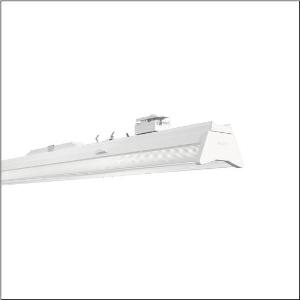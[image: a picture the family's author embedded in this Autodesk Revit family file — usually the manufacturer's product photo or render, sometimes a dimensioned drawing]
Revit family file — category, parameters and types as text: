
# Revit family: licross_r__21_performance_mo_52td167n485g_efc6
name_source: partatom
category: Lighting Fixtures
units: mm (PartAtom-declared; Revit-internal decimal feet)

## family parameters
Cut with Voids When Loaded = No
Host = Face
Light Source = No
Part Type = Normal
Room Calculation Point = No
Round Connector Dimension = Use Diameter
Shared = No

## types (1)
- Licross® 21 Performance MO (1 x LED, 8720 lm, 47.9 W, 4000K)
    Apparent Load = 48 VA
    CIE Flux Codes = 66 88 96 79 100
    Color Rendering = 80
    Color Temperature = 4000K
    Default Elevation = 1800 mm
    Description = Licross® 21 Performance MO, luminaire insert, of sheet steel, galvanised, coil coated, white, length: 1.500mm, width: 120mm, height: 123mm, LED rated luminous flux: 8.720lm, light colour: 840, control gear: ON/OFF, with plug, 3-pole, with phase selection, mains connection: 220..240V, AC, 50/60Hz, rated input power: 48W, halogen-free wiring, primary light control with lens, of plastic, primary optical cover: cover, of PMMA, light emission: direct/indirect distribution, primary light characteristic: symmetric, protection rating (complete): IP54, insulation class (complete): insulation class I (protective earthing), certification: CE, ENEC, UKCA, protection symbol: D if used in an environment with non-conductive dust loads with corresponding accessories, impact resistance: IK06, permissible ambient temperature for indoor applications: -35..+45°C, corresponds to IFS (International Featured Standards) requirements for safety and quality in the food industry, reducing of maximum allowable ambient temperature of 5°C with ceiling mounting, LABS conformity tested according to VDMA 24364:2018-05, packaging unit: 1 piece
    Height = 114 mm
    Lamp = 1 x LED
    Lamp Light Flux = 8720 lm
    Lamp Power = 47.9 W
    Lamp count = 1
    Length = 1500 mm
    Luminous efficacy = 182 lm/W
    Manufacturer = Siteco
    ModVariant = No
    Model = 52TD167N485G
    Mounting Place = Ceiling
    Mounting Type = Pendant
    Number of Poles = 1
    OnlyDefault = Yes
    Power Factor = 1
    Product Name = Licross® 21 Performance MO
    Product group = luminaire insert
    ProductGroupID = 901
    Protection Class = Protection class I
    Protection Degree = IP 54
    RLX_Detail_Level = 1
    RLX_Emergency_Light_Flux = 0 lm
    RLX_Emergency_Type = 0
    RLX_Emergency_Type_DB = No
    RlxData = <blob elided: 30365 chars, md5=98e7a5a4>
    Socket = socket
    Standby Power = 0 W
    System Light Flux = 8720 lm
    System Power = 48 W
    Type Comments = Product without accessories
    Type Image = l_1256138.jpg
    URL = http://relux.com
    VarID = ---
    Voltage = 0 V
    Weight = 0.00 kg
    Width = 120 mm

## geometry (parser evidence)
native form markers: Blend x4, Sweep x14
no freeform markers — native parametric forms only
